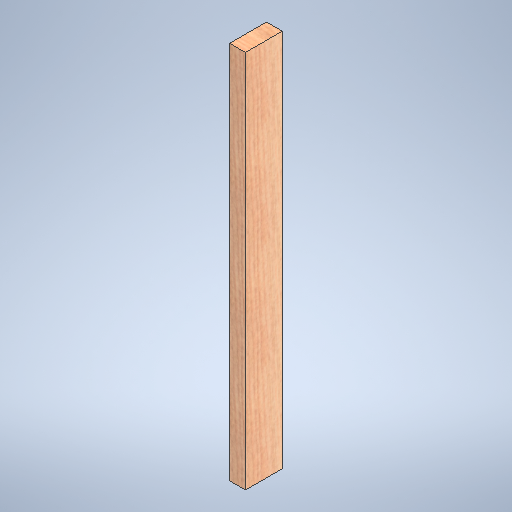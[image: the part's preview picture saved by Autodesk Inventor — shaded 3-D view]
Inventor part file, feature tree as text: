
AUTODESK INVENTOR PART (.ipt)
format: ipt  version: 2025.1 (Build 291241020, 241B)  size: 470,528 bytes
history: native  units: in
note: dims shown in document units (in); Inventor stores cm internally (conversion verified against a paired STEP export)
features: extrude x1, sketch x1
ambient origin geometry x8: Origin, YZ Plane, XZ Plane, XY Plane, X Axis, Y Axis, Z Axis, Center Point
bodies: Solid1 (feature_tree)
feature tree (2):
  extrude  "Extrusion1"  Depth=1.5in
  sketch  "Sketch1"  dims[d0=3.5in d1=1.5in d2=35.9375in d3=0.0in]
